# Revit family: 3039983 Lighting Fixture_Sylvania_Lumina Curve LED_Wall Mounted
name_source: partatom
category: Lighting Fixtures
revit_build: Autodesk Revit 2017 (Build: 20190507_1515(x64)
units: mm (PartAtom-declared; Revit-internal decimal feet)

## family parameters
Cut with Voids When Loaded = No
Host = Face
Light Source = Yes
OmniClass Number = 23.80.70.11.17
OmniClass Title = Specialized Lighting by Location or Use
Part Type = Normal
Room Calculation Point = No
Round Connector Dimension = Use Diameter
Shared = No

## types (1)
- Lumina Curve LED 2700K
    Accessory Material = Aluminum_Sylvania_Curve LED_White_RAL 9016
    Accessory Width = 78 mm  [stored 0.255906 ft]
    Apparent Load = 6 VA
    Assembly Code = D5020200
    Body Material = Aluminum_Sylvania_Curve LED_White_RAL 9016
    Color Filter = 16777215
    Default Elevation = 0 mm  [stored 0 ft]
    Description = Lumina LED is a new range of ambient & decorative LED wall lights. Consisting of multiple decorative styles, they are suitable for use in any hospitality or residential application such as reception areas, hallways and lounge spaces. Lumina LED offers a selection of different styles to suit multiple applications. With a 2,700K colour temperature it provides a soft and ambient lighting effect. Lumina LED provides direct/indirect ambient light with an efficacy of up to 87lm/W; up to 50% more energy efficient than equivalent products using traditional lamp sources.
    Dimming Lamp Color Temperature Shift = <None>
    Drive Current = 500mA
    Electrical Protection = Class II
    Emit Shape Visible in Rendering = No
    Emit from Circle Diameter = 6.5 mm
    Energy Class = A++, A+, A
    Height = 67 mm
    IP Rating = IP20
    Lamp = LED
    Length = 188 mm  [stored 0.616798 ft]
    Life = 30 000h
    Light Distribution = Direct/Indirect
    Manufacturer = Feilo Sylvania
    Model = 3039983 Lumina Curve LED 2700K
    Mounting Length = 110 mm  [stored 0.360892 ft]
    Photometric Web File = 3039983_LuminaCurveLED2700K-183046.ies
    Product Family = Lumina LED
    Product Page URL = http://www.sylvania-lighting.com
    Tilt Angle = -90.00°
    URL = http://www.sylvania-lighting.com
    Voltage = 240 V
    Voltage Comments = UNV (Universal Voltage; 100-240 Volt)
    Width = 104 mm

note: [stored X ft] marks values corroborated as IEEE doubles in the binary element streams (Revit-internal decimal feet)

## geometry (parser evidence)
native form markers: Blend x2, Sweep x1
no freeform markers — native parametric forms only
